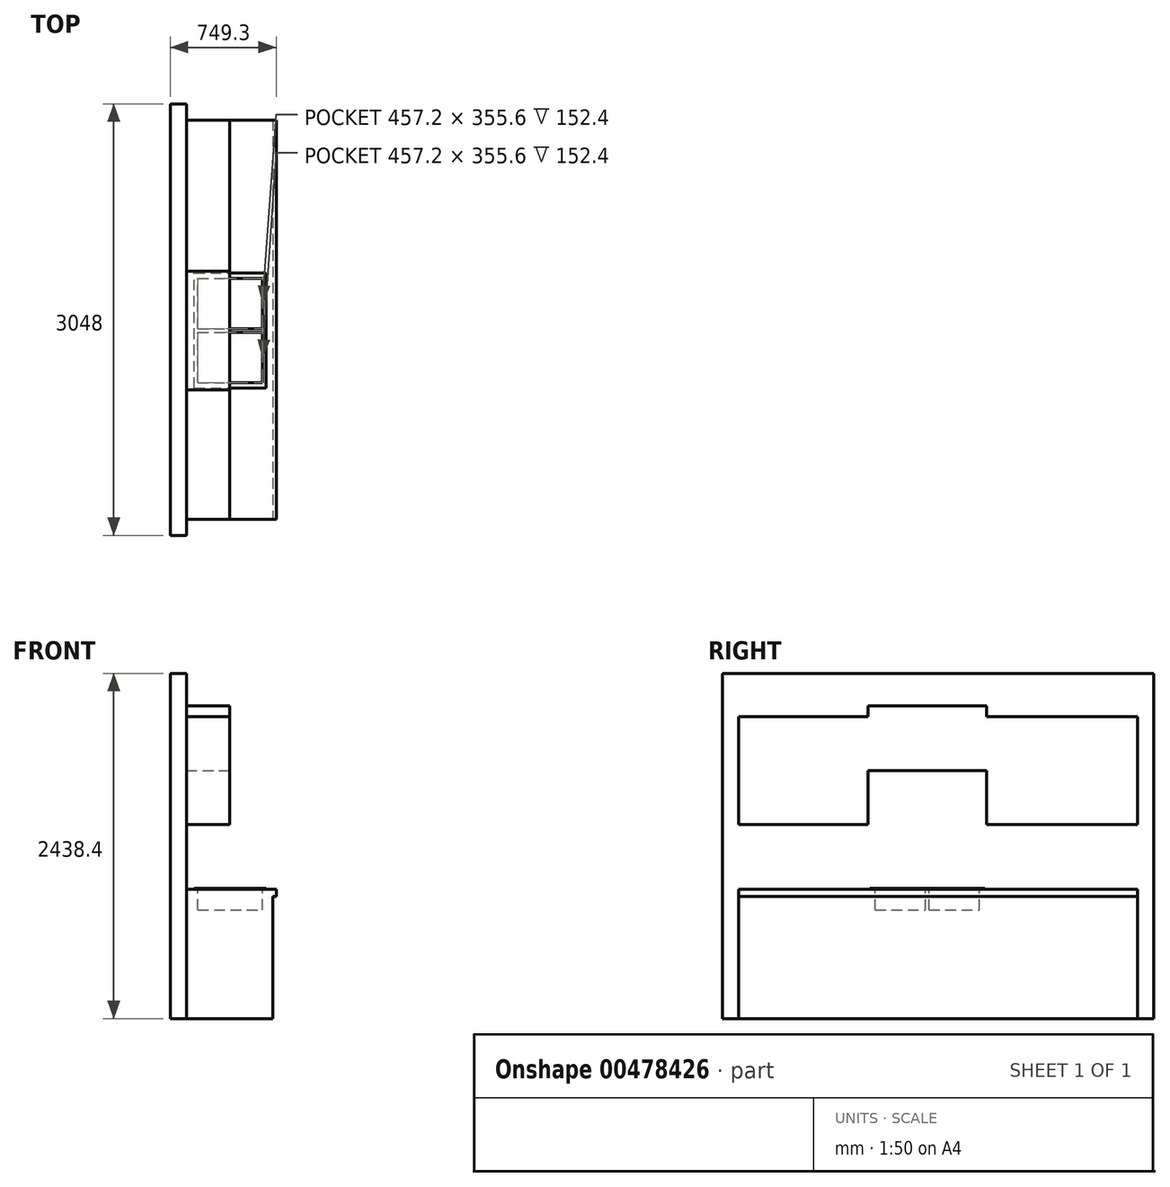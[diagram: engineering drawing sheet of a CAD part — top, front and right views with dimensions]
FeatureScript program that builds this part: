
annotation { "Feature Type Name" : "Feature", "Feature Type Description" : "" }
export const myFeature = defineFeature(function(context is Context, id is Id, definition is map)
    precondition{}
    {
        {
            var Q0;
            Q0=qCreatedBy(makeId("Top.planeOp"),FACE);
            var sketch = newSketch(context, id + "F0", { "sketchPlane" : qUnion([Q0])});
            skLineSegment(sketch, "E0.bottom", {"start": v(57.15, 1524) * mm, "end": v(-57.15, 1524) * mm});
            skLineSegment(sketch, "E0.top", {"start": v(57.15, -1524) * mm, "end": v(-57.15, -1524) * mm});
            skLineSegment(sketch, "E0.left", {"start": v(-57.15, 1524) * mm, "end": v(-57.15, -1524) * mm});
            skLineSegment(sketch, "E0.right", {"start": v(57.15, 1524) * mm, "end": v(57.15, -1524) * mm});
            skPoint(sketch, "E0.middle", {"position": v(0, 0) * mm});
            skSolve(sketch);
        }
        {
            var Q0;
            Q0 = qSketchRegion(id + "F0", true);
            extrude(context, id + "F1", {"entities" : qUnion([Q0]), "depth" : 2438.4 * mm});
        }
        {
            var Q0;
            Q0=makeQuery(id+"F1.opExtrude","SWEPT_FACE",FACE,{"disambiguationData":[OSD([sQuery(id+"F0.wireOp",EDGE,"E0.right")])]});
            var sketch = newSketch(context, id + "F2", { "sketchPlane" : qUnion([Q0])});
            skLineSegment(sketch, "E1.bottom", {"start": v(1409.7, 0) * mm, "end": v(-1409.7, 0) * mm});
            skLineSegment(sketch, "E1.top", {"start": v(1409.7, 863.6) * mm, "end": v(-1409.7, 863.6) * mm});
            skLineSegment(sketch, "E1.left", {"start": v(1409.7, 0) * mm, "end": v(1409.7, 863.6) * mm});
            skLineSegment(sketch, "E1.right", {"start": v(-1409.7, 0) * mm, "end": v(-1409.7, 863.6) * mm});
            skSolve(sketch);
        }
        {
            var Q0;
            Q0=makeQuery(id+"F2.imprint","IMPRINT",FACE,{"disambiguationData":[TD([[makeQuery(id+"F2.imprint","IMPRINT",EDGE,{"derivedFrom":sQuery(id+"F2.wireOp",EDGE,"E1.bottom")}),-1.0]])]});
            extrude(context, id + "F3", {"entities" : qUnion([Q0]), "operationType" : NewBodyOperationType.ADD, "depth" : 609.6 * mm});
        }
        {
            var Q0;
            Q0=makeQuery(id+"F1.opExtrude","SWEPT_FACE",FACE,{"disambiguationData":[OSD([sQuery(id+"F0.wireOp",EDGE,"E0.right")])]});
            var sketch = newSketch(context, id + "F4", { "sketchPlane" : qUnion([Q0])});
            skLineSegment(sketch, "E2.bottom", {"start": v(-1409.7, 1371.6) * mm, "end": v(1409.7, 1371.6) * mm});
            skLineSegment(sketch, "E2.top", {"start": v(-1409.7, 2133.6) * mm, "end": v(1409.7, 2133.6) * mm});
            skLineSegment(sketch, "E2.left", {"start": v(-1409.7, 1371.6) * mm, "end": v(-1409.7, 2133.6) * mm});
            skLineSegment(sketch, "E2.right", {"start": v(1409.7, 1371.6) * mm, "end": v(1409.7, 2133.6) * mm});
            skSolve(sketch);
        }
        {
            var Q0;
            Q0=makeQuery(id+"F4.imprint","IMPRINT",FACE,{"disambiguationData":[TD([[makeQuery(id+"F4.imprint","IMPRINT",EDGE,{"derivedFrom":sQuery(id+"F4.wireOp",EDGE,"E2.bottom")}),1.0]])]});
            extrude(context, id + "F5", {"entities" : qUnion([Q0]), "operationType" : NewBodyOperationType.ADD, "depth" : 304.8 * mm});
        }
        {
            var Q0;
            Q0=makeQuery(id+"F5.opExtrude","CAP_FACE",FACE,{"disambiguationData":[OSD([sQuery(id+"F4.wireOp",EDGE,"E2.bottom"),sQuery(id+"F4.wireOp",EDGE,"E2.top"),sQuery(id+"F4.wireOp",EDGE,"E2.left"),sQuery(id+"F4.wireOp",EDGE,"E2.right")])],"isStart":false});
            var sketch = newSketch(context, id + "F6", { "sketchPlane" : qUnion([Q0])});
            skLineSegment(sketch, "E3.bottom", {"start": v(-495.3, 1371.6) * mm, "end": v(342.9, 1371.6) * mm});
            skLineSegment(sketch, "E3.top", {"start": v(-495.3, 1752.6) * mm, "end": v(342.9, 1752.6) * mm});
            skLineSegment(sketch, "E3.left", {"start": v(-495.3, 1371.6) * mm, "end": v(-495.3, 1752.6) * mm});
            skLineSegment(sketch, "E3.right", {"start": v(342.9, 1371.6) * mm, "end": v(342.9, 1752.6) * mm});
            skSolve(sketch);
        }
        {
            var Q0;
            Q0=makeQuery(id+"F6.imprint","IMPRINT",FACE,{"disambiguationData":[TD([[makeQuery(id+"F6.imprint","IMPRINT",EDGE,{"derivedFrom":sQuery(id+"F6.wireOp",EDGE,"E3.bottom")}),1.0]])]});
            extrude(context, id + "F7", {"entities" : qUnion([Q0]), "operationType" : NewBodyOperationType.REMOVE, "oppositeDirection" : true, "depth" : 304.8 * mm});
        }
        {
            var Q0;
            Q0=makeQuery(id+"F5.opExtrude","SWEPT_FACE",FACE,{"disambiguationData":[OSD([sQuery(id+"F4.wireOp",EDGE,"E2.top")])]});
            var sketch = newSketch(context, id + "F8", { "sketchPlane" : qUnion([Q0])});
            skLineSegment(sketch, "E4.bottom", {"start": v(361.95, 342.9) * mm, "end": v(57.15, 342.9) * mm});
            skLineSegment(sketch, "E4.top", {"start": v(361.95, -495.3) * mm, "end": v(57.15, -495.3) * mm});
            skLineSegment(sketch, "E4.left", {"start": v(361.95, 342.9) * mm, "end": v(361.95, -495.3) * mm});
            skLineSegment(sketch, "E4.right", {"start": v(57.15, 342.9) * mm, "end": v(57.15, -495.3) * mm});
            skSolve(sketch);
        }
        {
            var Q0;
            Q0=makeQuery(id+"F8.imprint","IMPRINT",FACE,{"disambiguationData":[TD([[makeQuery(id+"F8.imprint","IMPRINT",EDGE,{"derivedFrom":sQuery(id+"F8.wireOp",EDGE,"E4.bottom")}),1.0]])]});
            extrude(context, id + "F9", {"entities" : qUnion([Q0]), "operationType" : NewBodyOperationType.ADD, "depth" : 76.2 * mm});
        }
        {
            var Q0;
            Q0=makeQuery(id+"F3.opExtrude","SWEPT_FACE",FACE,{"disambiguationData":[OSD([sQuery(id+"F2.wireOp",EDGE,"E1.top")])]});
            var sketch = newSketch(context, id + "F10", { "sketchPlane" : qUnion([Q0])});
            skLineSegment(sketch, "E5.bottom", {"start": v(57.15, -1409.7) * mm, "end": v(692.15, -1409.7) * mm});
            skLineSegment(sketch, "E5.top", {"start": v(57.15, 1409.7) * mm, "end": v(692.15, 1409.7) * mm});
            skLineSegment(sketch, "E5.left", {"start": v(57.15, -1409.7) * mm, "end": v(57.15, 1409.7) * mm});
            skLineSegment(sketch, "E5.right", {"start": v(692.15, -1409.7) * mm, "end": v(692.15, 1409.7) * mm});
            skSolve(sketch);
        }
        {
            var Q0;
            Q0 = qSketchRegion(id + "F10", true);
            extrude(context, id + "F11", {"entities" : qUnion([Q0]), "operationType" : NewBodyOperationType.ADD, "depth" : 50.8 * mm});
        }
        {
            var Q0;
            Q0=makeQuery(id+"F11.opExtrude","CAP_FACE",FACE,{"disambiguationData":[OSD([sQuery(id+"F10.wireOp",EDGE,"E5.bottom"),sQuery(id+"F10.wireOp",EDGE,"E5.top"),sQuery(id+"F10.wireOp",EDGE,"E5.left"),sQuery(id+"F10.wireOp",EDGE,"E5.right")])],"isStart":false});
            var sketch = newSketch(context, id + "F12", { "sketchPlane" : qUnion([Q0])});
            skLineSegment(sketch, "E6.bottom", {"start": v(113.37, -482.6) * mm, "end": v(621.37, -482.6) * mm});
            skLineSegment(sketch, "E6.top", {"start": v(113.37, 330.2) * mm, "end": v(621.37, 330.2) * mm});
            skLineSegment(sketch, "E6.left", {"start": v(113.37, -482.6) * mm, "end": v(113.37, 330.2) * mm});
            skLineSegment(sketch, "E6.right", {"start": v(621.37, -482.6) * mm, "end": v(621.37, 330.2) * mm});
            skSolve(sketch);
        }
        {
            var Q0;
            Q0=makeQuery(id+"F12.imprint","IMPRINT",FACE,{"disambiguationData":[TD([[makeQuery(id+"F12.imprint","IMPRINT",EDGE,{"derivedFrom":sQuery(id+"F12.wireOp",EDGE,"E6.bottom")}),1.0]])]});
            extrude(context, id + "F13", {"entities" : qUnion([Q0]), "operationType" : NewBodyOperationType.ADD, "depth" : 6.35 * mm});
        }
        {
            var Q0;
            Q0=makeQuery(id+"F13.opExtrude","CAP_FACE",FACE,{"disambiguationData":[OSD([sQuery(id+"F12.wireOp",EDGE,"E6.bottom"),sQuery(id+"F12.wireOp",EDGE,"E6.top"),sQuery(id+"F12.wireOp",EDGE,"E6.left"),sQuery(id+"F12.wireOp",EDGE,"E6.right")])],"isStart":false});
            var sketch = newSketch(context, id + "F14", { "sketchPlane" : qUnion([Q0])});
            skLineSegment(sketch, "E7.bottom", {"start": v(138.77, -444.5) * mm, "end": v(595.97, -444.5) * mm});
            skLineSegment(sketch, "E7.top", {"start": v(138.77, -88.9) * mm, "end": v(595.97, -88.9) * mm});
            skLineSegment(sketch, "E7.left", {"start": v(138.77, -444.5) * mm, "end": v(138.77, -88.9) * mm});
            skLineSegment(sketch, "E7.right", {"start": v(595.97, -444.5) * mm, "end": v(595.97, -88.9) * mm});
            skLineSegment(sketch, "E8.bottom", {"start": v(138.77, -63.5) * mm, "end": v(595.97, -63.5) * mm});
            skLineSegment(sketch, "E8.top", {"start": v(138.77, 292.1) * mm, "end": v(595.97, 292.1) * mm});
            skLineSegment(sketch, "E8.left", {"start": v(138.77, -63.5) * mm, "end": v(138.77, 292.1) * mm});
            skLineSegment(sketch, "E8.right", {"start": v(595.97, -63.5) * mm, "end": v(595.97, 292.1) * mm});
            skSolve(sketch);
        }
        {
            var Q0;
            Q0=makeQuery(id+"F14.imprint","IMPRINT",FACE,{"disambiguationData":[TD([[makeQuery(id+"F14.imprint","IMPRINT",EDGE,{"derivedFrom":sQuery(id+"F14.wireOp",EDGE,"E7.bottom")}),1.0]])]});
            var Q1;
            Q1=makeQuery(id+"F14.imprint","IMPRINT",FACE,{"disambiguationData":[TD([[makeQuery(id+"F14.imprint","IMPRINT",EDGE,{"derivedFrom":sQuery(id+"F14.wireOp",EDGE,"E8.bottom")}),1.0]])]});
            extrude(context, id + "F15", {"entities" : qUnion([Q0, Q1]), "operationType" : NewBodyOperationType.REMOVE, "oppositeDirection" : true, "depth" : 152.4 * mm});
        }
    });
